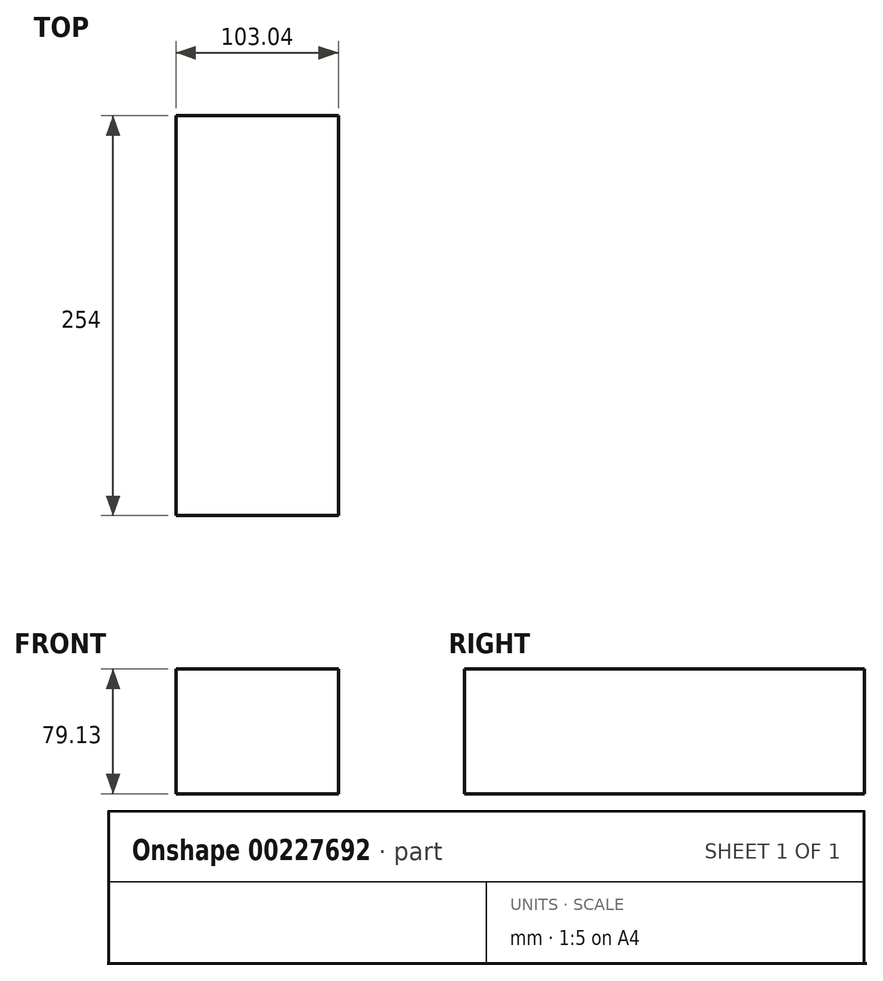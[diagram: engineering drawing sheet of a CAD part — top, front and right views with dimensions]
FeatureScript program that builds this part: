
annotation { "Feature Type Name" : "Feature", "Feature Type Description" : "" }
export const myFeature = defineFeature(function(context is Context, id is Id, definition is map)
    precondition{}
    {
        {
            var Q0;
            Q0=qCreatedBy(makeId("Front.planeOp"),FACE);
            var sketch = newSketch(context, id + "F0", { "sketchPlane" : qUnion([Q0])});
            skLineSegment(sketch, "E0.bottom", {"start": v(-49.82, 38.58) * mm, "end": v(53.22, 38.58) * mm});
            skLineSegment(sketch, "E0.top", {"start": v(-49.82, -40.55) * mm, "end": v(53.22, -40.55) * mm});
            skLineSegment(sketch, "E0.left", {"start": v(-49.82, 38.58) * mm, "end": v(-49.82, -40.55) * mm});
            skLineSegment(sketch, "E0.right", {"start": v(53.22, 38.58) * mm, "end": v(53.22, -40.55) * mm});
            skSolve(sketch);
        }
        {
            var Q0;
            Q0=makeQuery(id+"F0.imprint","IMPRINT",FACE,{"disambiguationData":[TD([[makeQuery(id+"F0.imprint","IMPRINT",EDGE,{"derivedFrom":sQuery(id+"F0.wireOp",EDGE,"E0.bottom")}),-1.0]])]});
            extrude(context, id + "F1", {"entities" : qUnion([Q0]), "depth" : 254 * mm});
        }
    });
